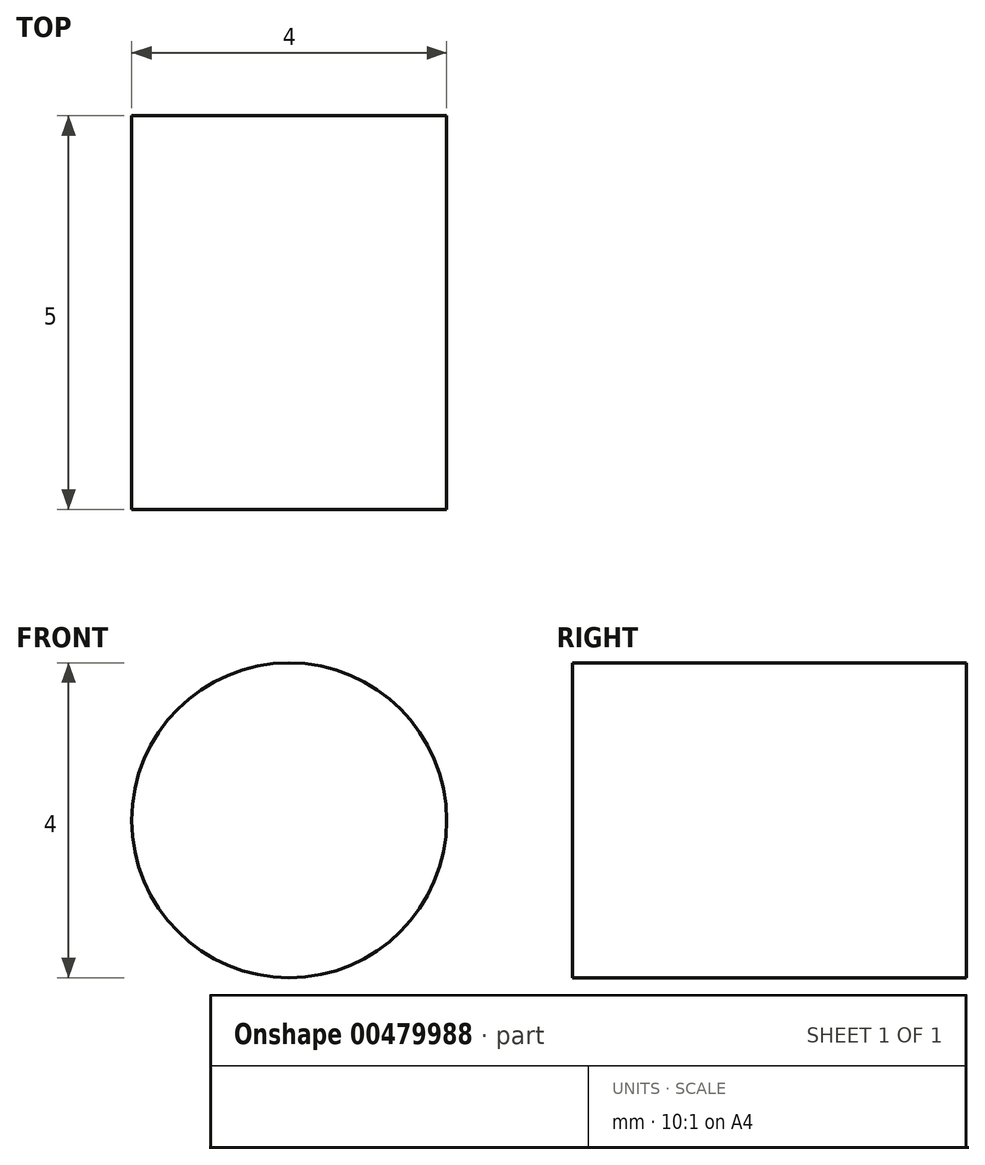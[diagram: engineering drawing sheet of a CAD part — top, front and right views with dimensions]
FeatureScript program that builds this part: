
annotation { "Feature Type Name" : "Feature", "Feature Type Description" : "" }
export const myFeature = defineFeature(function(context is Context, id is Id, definition is map)
    precondition{}
    {
        {
            var Q0;
            Q0=qCreatedBy(makeId("Front.planeOp"),FACE);
            var sketch = newSketch(context, id + "F0", { "sketchPlane" : qUnion([Q0])});
            skCircle(sketch, "E0", {"center": v(0, 0) * mm, "radius": 2 * mm});
            skSolve(sketch);
        }
        {
            var Q0;
            Q0=makeQuery(id+"F0.imprint","IMPRINT",FACE,{"disambiguationData":[TD([[makeQuery(id+"F0.imprint","IMPRINT",EDGE,{"derivedFrom":sQuery(id+"F0.wireOp",EDGE,"E0")}),1.0]])]});
            extrude(context, id + "F1", {"entities" : qUnion([Q0]), "depth" : 5 * mm});
        }
    });
